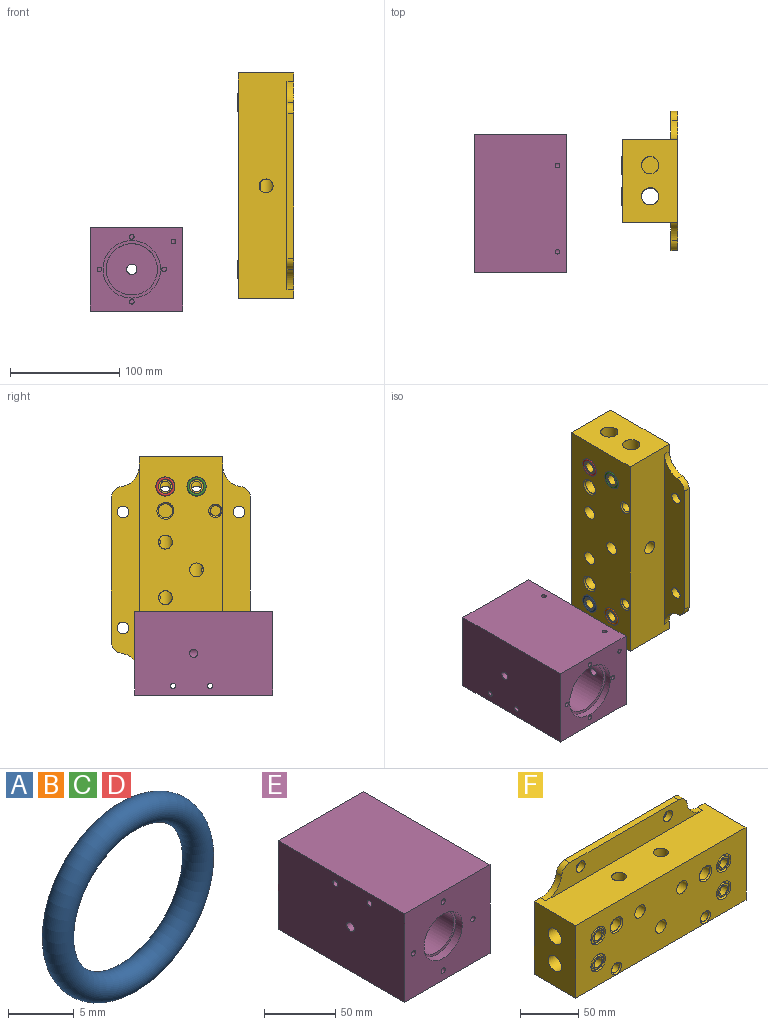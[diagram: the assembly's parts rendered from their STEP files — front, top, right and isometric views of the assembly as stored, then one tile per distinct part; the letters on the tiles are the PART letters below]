
ASSEMBLY  parts=6 mates=5
PART A: 1 faces, bbox 18.9x2.4x18.9 mm
  f0: torus R=7.54mm, axis (0,-1,0), area 354.4mm2
PART B: same geometry as A
PART C: same geometry as A
PART D: same geometry as A
PART E: 42 faces, bbox 84.7x126.1x76.2 mm
  f0: cylinder r=2.12mm len=12.7mm, axis (0,0,-1), area 151mm2, adj f8,f22,f23
  f1: cylinder r=3.7mm len=29.87mm, axis (1,0,0), area 675.7mm2, adj f5,f19,f21
  f2: cylinder r=3.7mm len=23.41mm, axis (1,0,0), area 526.6mm2, adj f4,f19,f20
  f3: cylinder r=4.76mm len=14.33mm, axis (0,-1,0), area 381.4mm2, adj f13,f16,f18
  f4: cylinder r=23.45mm len=58mm, axis (0,1,0), area 8459.7mm2, adj f2,f11,f13,f17
  f5: cylinder r=17.1mm len=41.06mm, axis (0,-1,0), area 4369.1mm2, adj f1,f14,f16
  f6: plane 126.09x84.67mm, normal (0,0,1), area 10675.6mm2, adj f7,f9,f10,f19
  f7: plane 126.09x76.2mm, normal (-1,0,0), area 9530.9mm2, adj f6,f8,f9,f10,f18,f40,f41
  f8: plane 126.09x84.67mm, normal (0,0,-1), area 10647.5mm2, adj f0,f7,f9,f10,f19,f21
  f9: plane 84.67x76.2mm, normal (0,-1,0), area 5255.1mm2, adj f6,f7,f8,f15,f19,f32,f34,f36
  f10: plane 84.67x76.2mm, normal (0,1,0), area 4216.9mm2, adj f6,f7,f8,f12,f19,f23,f24,f26
  f11: plane 52.49x52.49mm, normal (0,1,0), area 436.2mm2, adj f4,f12
  f12: cylinder r=26.25mm len=52.49mm, axis (0,1,0), area 1047.2mm2, adj f10,f11
  f13: plane 46.91x46.91mm, normal (0,1,0), area 1656.7mm2, adj f3,f4
  f14: plane 38.1x38.1mm, normal (0,-1,0), area 221.2mm2, adj f5,f15
  f15: cylinder r=19.05mm len=38.1mm, axis (0,-1,0), area 760mm2, adj f9,f14
  f16: plane 34.21x34.21mm, normal (0,-1,0), area 847.6mm2, adj f3,f5
  f17: cylinder r=3.7mm len=23.41mm, axis (1,0,0), area 541.4mm2, adj f4,f19
  f18: cylinder r=3.7mm len=35.11mm, axis (-1,0,0), area 795.3mm2, adj f3,f7
  f19: plane 126.09x76.2mm, normal (1,0,0), area 9444.7mm2, adj f1,f2,f6,f8,f9,f10,f17,f40
  f20: cylinder r=2.12mm len=22.36mm, axis (0,0,-1), area 274.9mm2, adj f2,f22,f23
  f21: cylinder r=2.12mm len=35.08mm, axis (0,0,-1), area 443.8mm2, adj f1,f8,f22
  f22: cylinder r=2.12mm len=78.79mm, axis (0,1,0), area 1012mm2, adj f0,f20,f21
  f23: cylinder r=2.12mm len=19.05mm, axis (0,1,0), area 235.4mm2, adj f0,f10,f20
  f24: cylinder r=2.12mm len=6.35mm, axis (0,1,0), area 84.4mm2, adj f10,f25
  f25: plane 4.23x4.23mm, normal (0,1,0), area 14.1mm2, adj f24
  f26: cylinder r=2.12mm len=6.35mm, axis (0,1,0), area 84.4mm2, adj f10,f27
  f27: plane 4.23x4.23mm, normal (0,1,0), area 14.1mm2, adj f26
  f28: cylinder r=2.12mm len=6.35mm, axis (0,1,0), area 84.4mm2, adj f10,f29
  f29: plane 4.23x4.23mm, normal (0,1,0), area 14.1mm2, adj f28
  f30: cylinder r=2.12mm len=6.35mm, axis (0,1,0), area 84.4mm2, adj f10,f31
  f31: plane 4.23x4.23mm, normal (0,1,0), area 14.1mm2, adj f30
  f32: cylinder r=2.12mm len=6.35mm, axis (0,-1,0), area 84.4mm2, adj f9,f33
  f33: plane 4.23x4.23mm, normal (0,-1,0), area 14.1mm2, adj f32
  f34: cylinder r=2.12mm len=6.35mm, axis (0,-1,0), area 84.4mm2, adj f9,f35
  f35: plane 4.23x4.23mm, normal (0,-1,0), area 14.1mm2, adj f34
  f36: cylinder r=2.12mm len=6.35mm, axis (0,-1,0), area 84.4mm2, adj f9,f37
  f37: plane 4.23x4.23mm, normal (0,-1,0), area 14.1mm2, adj f36
  f38: cylinder r=2.12mm len=6.35mm, axis (0,-1,0), area 84.4mm2, adj f9,f39
  f39: plane 4.23x4.23mm, normal (0,-1,0), area 14.1mm2, adj f38
  f40: cylinder r=2.33mm len=84.67mm, axis (1,0,0), area 1238.6mm2, adj f7,f19
  f41: cylinder r=2.33mm len=84.67mm, axis (1,0,0), area 1238.6mm2, adj f7,f19
PART F: 77 faces, bbox 206.4x50.8x127 mm
  f0: plane 12.7x12.7mm, normal (0,-1,0), area 55.4mm2, adj f19,f74
  f1: plane 12.7x12.7mm, normal (0,-1,0), area 55.4mm2, adj f20,f71
  f2: plane 12.7x12.7mm, normal (0,-1,0), area 55.4mm2, adj f18,f68
  f3: plane 12.7x12.7mm, normal (0,-1,0), area 55.4mm2, adj f15,f65
  f4: cylinder r=6.58mm len=18.67mm, axis (0,1,0), area 694.4mm2, adj f24,f51
  f5: cylinder r=6.58mm len=18.67mm, axis (0,1,0), area 694.5mm2, adj f22,f49
  f6: cylinder r=6.58mm len=18.67mm, axis (0,1,0), area 694.5mm2, adj f21,f47
  f7: cylinder r=6.58mm len=18.67mm, axis (0,1,0), area 694.5mm2, adj f21,f45
  f8: plane 76.2x50.8mm, normal (-1,0,0), area 3475.1mm2, adj f9,f11,f12,f13,f21,f22
  f9: plane 206.38x50.8mm, normal (0,0,-1), area 9150.7mm2, adj f8,f10,f12,f13,f29,f34,f35,f44
  f10: plane 76.2x50.8mm, normal (1,0,0), area 3475.1mm2, adj f9,f11,f12,f13,f21,f24
  f11: plane 206.38x50.8mm, normal (0,0,1), area 9024mm2, adj f8,f10,f12,f13,f27,f36,f37,f42
  f12: plane 206.38x127mm, normal (0,1,0), area 22150.9mm2, adj f8,f9,f10,f11,f26,f28,f30,f31
  f13: plane 206.38x76.2mm, normal (0,-1,0), area 13780.6mm2, adj f8,f9,f10,f11,f14,f16,f17,f61
  f14: cylinder r=6.35mm len=20.64mm, axis (0,-1,0), area 749.7mm2, adj f13,f21,f44
  f15: cylinder r=4.76mm len=19.05mm, axis (0,-1,0), area 545.7mm2, adj f3,f24
  f16: cylinder r=6.35mm len=20.64mm, axis (0,-1,0), area 749.7mm2, adj f13,f24,f42
  f17: cylinder r=6.35mm len=20.64mm, axis (0,-1,0), area 749.7mm2, adj f13,f22,f43
  f18: cylinder r=4.76mm len=19.05mm, axis (0,-1,0), area 545.6mm2, adj f2,f22
  f19: cylinder r=4.76mm len=19.05mm, axis (0,-1,0), area 545.7mm2, adj f0,f21
  f20: cylinder r=4.76mm len=19.05mm, axis (0,-1,0), area 545.7mm2, adj f1,f21
  f21: cylinder r=7.94mm len=206.38mm, axis (-1,0,0), area 9564.9mm2, adj f6,f7,f8,f10,f14,f19,f20,f44
  f22: cylinder r=7.94mm len=88.9mm, axis (-1,0,0), area 3933.9mm2, adj f5,f8,f17,f18,f23,f43
  f23: plane 15.88x15.88mm, normal (-1,0,0), area 197.9mm2, adj f22
  f24: cylinder r=7.94mm len=88.9mm, axis (1,0,0), area 3933.7mm2, adj f4,f10,f15,f16,f25,f42
  f25: plane 15.88x15.88mm, normal (1,0,0), area 197.9mm2, adj f24
  f26: plane 132.08x6.35mm, normal (0,0,1), area 838.7mm2, adj f12,f27,f30,f31
  f27: plane 190x25.4mm, normal (0,-1,0), area 3791.8mm2, adj f11,f26,f30,f31,f36,f37,f40,f41
  f28: plane 132.08x6.35mm, normal (0,0,-1), area 838.7mm2, adj f12,f29,f32,f33
  f29: plane 190x25.4mm, normal (0,-1,0), area 3791.8mm2, adj f9,f28,f32,f33,f34,f35,f38,f39
  f30: cylinder r=10.16mm len=10.07mm, axis (0,1,0), area 92.9mm2, adj f12,f26,f27,f36
  f31: cylinder r=10.16mm len=10.07mm, axis (0,-1,0), area 92.9mm2, adj f12,f26,f27,f37
  f32: cylinder r=10.16mm len=10.07mm, axis (0,-1,0), area 92.9mm2, adj f12,f28,f29,f34
  f33: cylinder r=10.16mm len=10.07mm, axis (0,1,0), area 92.9mm2, adj f12,f28,f29,f35
  f34: cylinder r=19.05mm len=18.89mm, axis (0,-1,0), area 174.2mm2, adj f9,f12,f29,f32
  f35: cylinder r=19.05mm len=18.89mm, axis (0,1,0), area 174.2mm2, adj f9,f12,f29,f33
  f36: cylinder r=19.05mm len=18.89mm, axis (0,1,0), area 174.2mm2, adj f11,f12,f27,f30
  f37: cylinder r=19.05mm len=18.89mm, axis (0,-1,0), area 174.2mm2, adj f11,f12,f27,f31
  f38: cylinder r=5.38mm len=10.77mm, axis (0,1,0), area 214.8mm2, adj f12,f29
  f39: cylinder r=5.38mm len=10.77mm, axis (0,1,0), area 214.8mm2, adj f12,f29
  f40: cylinder r=5.38mm len=10.77mm, axis (0,1,0), area 214.8mm2, adj f12,f27
  f41: cylinder r=5.38mm len=10.77mm, axis (0,1,0), area 214.8mm2, adj f12,f27
  f42: cylinder r=6.35mm len=19.11mm, axis (0,0,1), area 688.9mm2, adj f11,f16,f24
  f43: cylinder r=6.35mm len=19.11mm, axis (0,0,1), area 688.9mm2, adj f11,f17,f22
  f44: cylinder r=6.35mm len=19.12mm, axis (0,0,-1), area 688.9mm2, adj f9,f14,f21
  f45: plane 19.2x19.2mm, normal (0,1,0), area 153.6mm2, adj f7,f46
  f46: cylinder r=9.6mm len=19.2mm, axis (0,1,0), area 137.9mm2, adj f12,f45
  f47: plane 19.2x19.2mm, normal (0,1,0), area 153.6mm2, adj f6,f48
  f48: cylinder r=9.6mm len=19.2mm, axis (0,1,0), area 137.9mm2, adj f12,f47
  f49: plane 19.2x19.2mm, normal (0,1,0), area 153.6mm2, adj f5,f50
  f50: cylinder r=9.6mm len=19.2mm, axis (0,1,0), area 137.9mm2, adj f12,f49
  f51: plane 19.2x19.2mm, normal (0,1,0), area 153.6mm2, adj f4,f52
  f52: cylinder r=9.6mm len=19.2mm, axis (0,1,0), area 137.9mm2, adj f12,f51
  f53: cylinder r=6.48mm len=12.95mm, axis (0,-1,0), area 335.9mm2, adj f54,f64
  f54: plane 12.95x12.95mm, normal (0,-1,0), area 131.8mm2, adj f53
  f55: cylinder r=4.76mm len=9.53mm, axis (0,-1,0), area 247mm2, adj f56,f62
  f56: plane 9.53x9.53mm, normal (0,-1,0), area 71.3mm2, adj f55
  f57: cylinder r=6.48mm len=12.95mm, axis (0,-1,0), area 335.9mm2, adj f58,f61
  f58: plane 12.95x12.95mm, normal (0,-1,0), area 131.8mm2, adj f57
  f59: cylinder r=4.76mm len=9.53mm, axis (0,-1,0), area 247mm2, adj f60,f63
  f60: plane 9.53x9.53mm, normal (0,-1,0), area 71.3mm2, adj f59
  f61: cone r=6.48mm half-angle=45deg, axis (0,-1,0), area 80.3mm2, adj f13,f57
  f62: cone r=4.76mm half-angle=45deg, axis (0,-1,0), area 60.9mm2, adj f13,f55
  f63: cone r=4.76mm half-angle=45deg, axis (0,-1,0), area 60.9mm2, adj f13,f59
  f64: cone r=6.48mm half-angle=45deg, axis (0,-1,0), area 80.3mm2, adj f13,f53
  f65: cylinder r=6.35mm len=12.7mm, axis (0,-1,0), area 94.2mm2, adj f3,f67
  f66: cylinder r=8.74mm len=17.48mm, axis (0,-1,0), area 129.7mm2, adj f13,f67
  f67: plane 17.48x17.48mm, normal (0,-1,0), area 113.2mm2, adj f65,f66
  f68: cylinder r=6.35mm len=12.7mm, axis (0,-1,0), area 94.2mm2, adj f2,f70
  f69: cylinder r=8.74mm len=17.48mm, axis (0,-1,0), area 129.7mm2, adj f13,f70
  f70: plane 17.48x17.48mm, normal (0,-1,0), area 113.2mm2, adj f68,f69
  f71: cylinder r=6.35mm len=12.7mm, axis (0,-1,0), area 94.2mm2, adj f1,f73
  f72: cylinder r=8.74mm len=17.48mm, axis (0,-1,0), area 129.7mm2, adj f13,f73
  f73: plane 17.48x17.48mm, normal (0,-1,0), area 113.2mm2, adj f71,f72
  f74: cylinder r=6.35mm len=12.7mm, axis (0,-1,0), area 94.2mm2, adj f0,f76
  f75: cylinder r=8.74mm len=17.48mm, axis (0,-1,0), area 129.7mm2, adj f13,f76
  f76: plane 17.48x17.48mm, normal (0,-1,0), area 113.2mm2, adj f74,f75
PLACE A rot(axis=(0,0,-1),90deg) t=(52.27,-87.46,-255.14)mm
PLACE B rot(axis=(0,0,-1),90deg) t=(52.19,-115.91,-255.14)mm
PLACE C rot(axis=(0,0,-1),90deg) t=(52.19,-115.91,-102.74)mm
PLACE D rot(axis=(0,0,-1),90deg) t=(52.27,-87.46,-102.74)mm
PLACE E rot(axis=(1,0,0),180deg) t=(-45.68,-185.33,-255.14)mm
PLACE F rot(axis=(-0.58,-0.58,-0.58),120deg) t=(51.69,-101.68,-178.94)mm fixed
MATE fastened F.f18 <-> A.f0  axis (-1,0,0) through (51.69,-87.46,-255.14)mm
MATE fastened F.f20 <-> B.f0  axis (-1,0,0) through (51.69,-115.91,-255.14)mm
MATE slider E.f1 <-> F.f18  axis (1,0,0) through (0.89,-87.46,-255.14)mm
MATE fastened F.f19 <-> C.f0  axis (-1,0,0) through (51.69,-115.91,-102.74)mm
MATE fastened F.f15 <-> D.f0  axis (-1,0,0) through (51.69,-87.46,-102.74)mm
